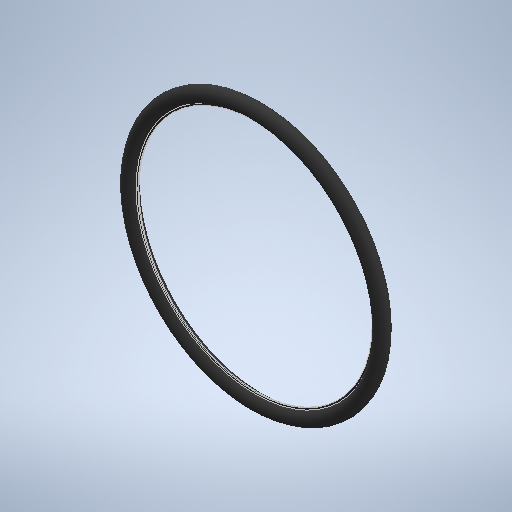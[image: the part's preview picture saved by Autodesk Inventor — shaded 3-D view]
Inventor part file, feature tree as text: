
AUTODESK INVENTOR PART (.ipt)
format: ipt  version: 2025 (Build 290162000, 162)  size: 296,448 bytes
history: native  units: in
note: dims shown in document units (in); Inventor stores cm internally (conversion verified against a paired STEP export)
features: extrude x1, sketch x1, revolve x1
ambient origin geometry x8: Origin, YZ Plane, XZ Plane, XY Plane, X Axis, Y Axis, Z Axis, Center Point
bodies: Solid1 (feature_tree)
feature tree (3):
  extrude  "Extrusion1"  [1 undecoded]
  sketch  "Sketch1"  dims[d0=0.0039in d1=0.0in]
  revolve  "Revolve1"  [1 undecoded]
note: 2 required parameter values undecoded (feature->parameter linkage not recoverable at this tier; creation-order binding heuristic only, values carry confidence <= 0.55)
